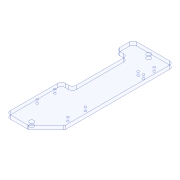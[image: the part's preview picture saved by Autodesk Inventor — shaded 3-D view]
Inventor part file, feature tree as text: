
AUTODESK INVENTOR PART (.ipt)
format: ipt  version: 2020 (Build 240168000, 168)  size: 140,800 bytes
history: mixed  units: mm
features: fillet x2, extrude x1, sketch x1, imported_body x1
ambient origin geometry x8: Origin, YZ Plane, XZ Plane, XY Plane, X Axis, Y Axis, Z Axis, Center Point
bodies: Solid1 (imported_parasolid)
feature tree (5):
  extrude  "Extrusion1"  Depth=10.0mm TaperAngle=0.0deg
  fillet  "Fillet1"  Radius=2.0mm
  sketch  "Sketch1"  dims[d0=11.0mm d1=10.0mm d2=0.0mm d3=2.0mm]
  fillet  "Fillet7"  [1 undecoded]
  imported_body  NMx_Import_Brep_tag  [imported B-rep: ~29 faces, bbox_mm=[55.0, 5.0, 173.0]]
note: 1 required parameter value undecoded (feature->parameter linkage not recoverable at this tier; creation-order binding heuristic only, values carry confidence <= 0.55)
